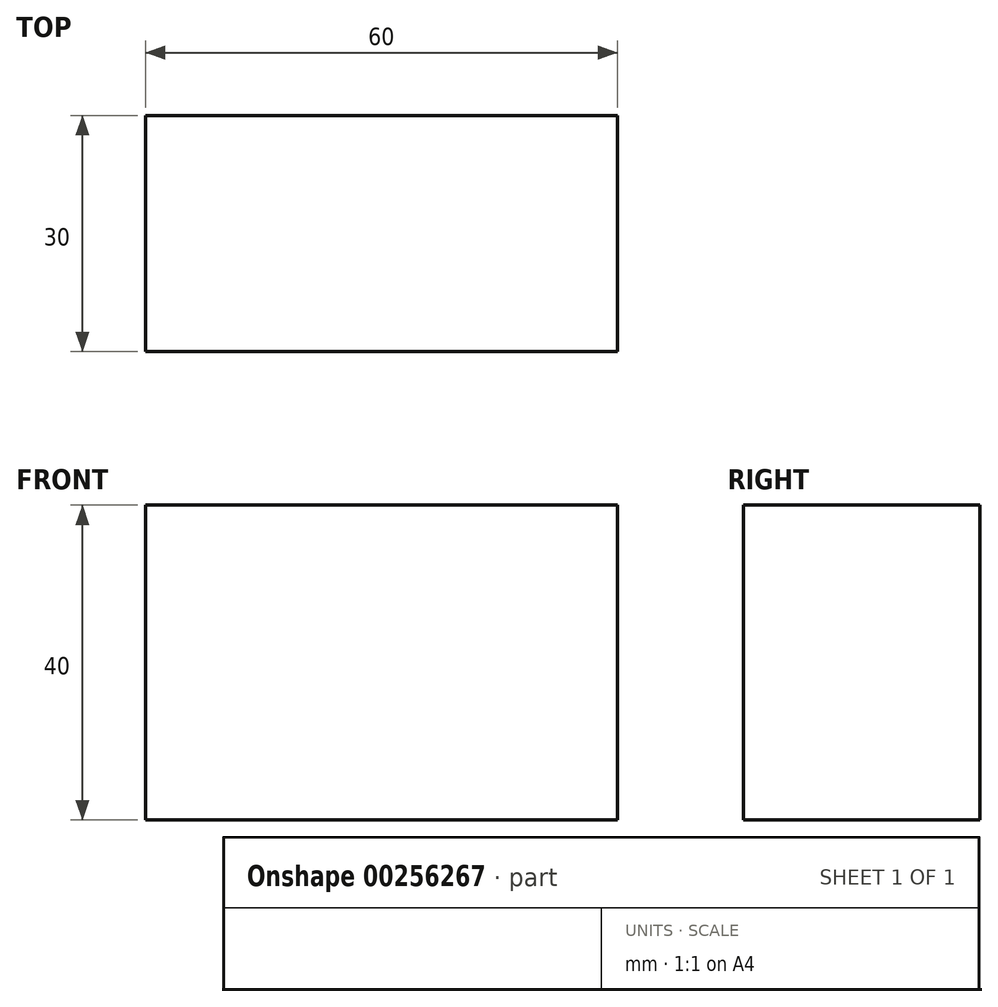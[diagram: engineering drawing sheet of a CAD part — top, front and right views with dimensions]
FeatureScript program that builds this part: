
annotation { "Feature Type Name" : "Feature", "Feature Type Description" : "" }
export const myFeature = defineFeature(function(context is Context, id is Id, definition is map)
    precondition{}
    {
        {
            var Q0;
            Q0=qCreatedBy(makeId("Front.planeOp"),FACE);
            var sketch = newSketch(context, id + "F0", { "sketchPlane" : qUnion([Q0])});
            skLineSegment(sketch, "E0.bottom", {"start": v(0, 0) * mm, "end": v(60, 0) * mm});
            skLineSegment(sketch, "E0.top", {"start": v(0, -40) * mm, "end": v(60, -40) * mm});
            skLineSegment(sketch, "E0.left", {"start": v(0, 0) * mm, "end": v(0, -40) * mm});
            skLineSegment(sketch, "E0.right", {"start": v(60, 0) * mm, "end": v(60, -40) * mm});
            skSolve(sketch);
        }
        {
            var Q0;
            Q0 = qSketchRegion(id + "F0", true);
            extrude(context, id + "F1", {"entities" : qUnion([Q0]), "depth" : 30 * mm});
        }
    });
